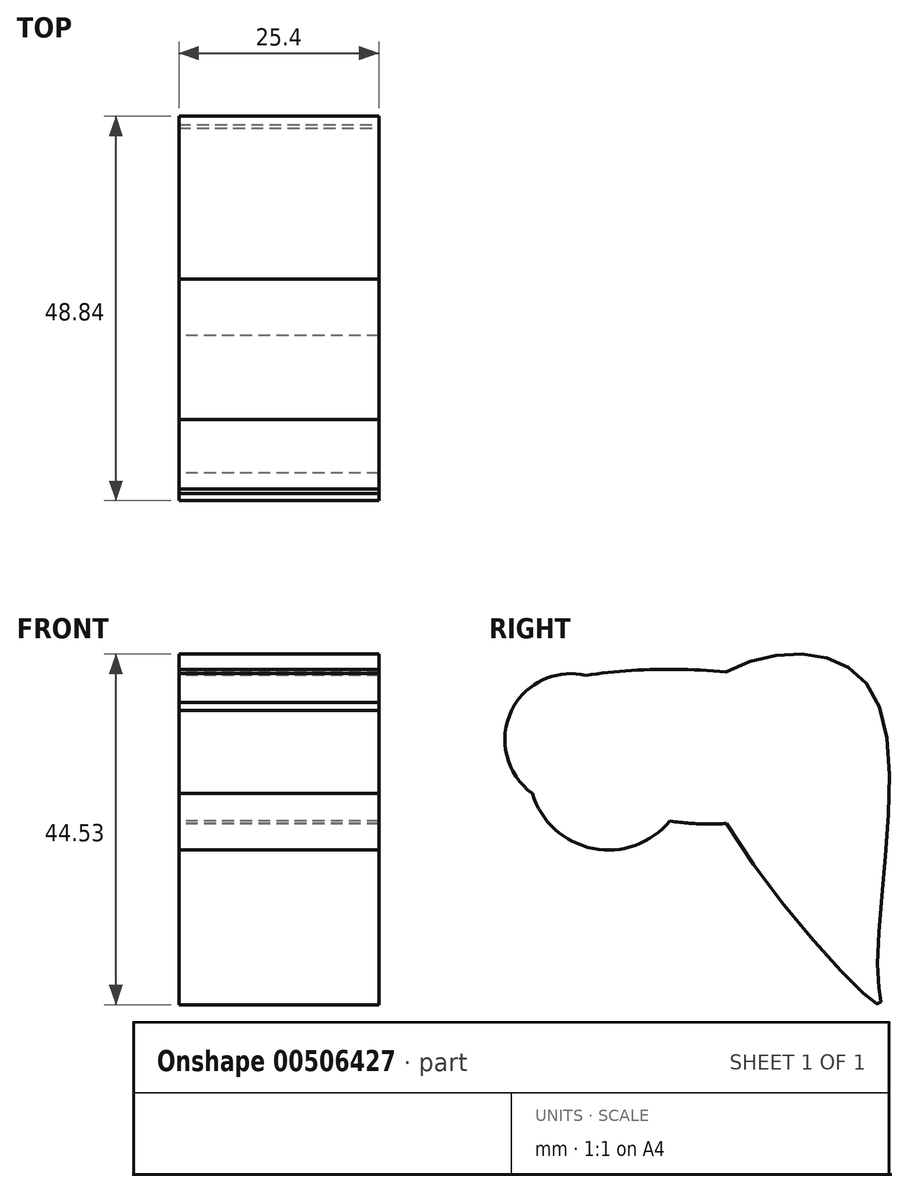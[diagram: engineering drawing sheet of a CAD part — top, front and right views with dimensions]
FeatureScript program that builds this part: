
annotation { "Feature Type Name" : "Feature", "Feature Type Description" : "" }
export const myFeature = defineFeature(function(context is Context, id is Id, definition is map)
    precondition{}
    {
        {
            var Q0;
            Q0=qCreatedBy(makeId("Right.planeOp"),FACE);
            var sketch = newSketch(context, id + "F0", { "sketchPlane" : qUnion([Q0])});
            skFitSpline(sketch, "E0", {"points": [v(-45.92, 38.32) * mm, v(-22.24, 22.9) * mm, v(0, 36.42) * mm, v(-45.92, 38.32) * mm]});
            skFitSpline(sketch, "E1", {"points": [v(-23.59, 33.6) * mm, v(-13.3, 44.24) * mm, v(0, 38.32) * mm, v(0, 3.47) * mm, v(0, 0) * mm, v(-23.59, 33.6) * mm]});
            skArc(sketch, "E2", {"start": v(-37.06, 41.8) * mm, "mid": v(-46.62, 37.08) * mm, "end": v(-43.88, 26.78) * mm});
            skArc(sketch, "E3", {"start": v(-44.15, 31.5) * mm, "mid": v(-36.83, 19.95) * mm, "end": v(-24.68, 26.26) * mm});
            skSolve(sketch);
        }
        {
            var Q0;
            Q0 = qSketchRegion(id + "F0", true);
            extrude(context, id + "F1", {"entities" : qUnion([Q0]), "depth" : 25.4 * mm});
        }
    });
